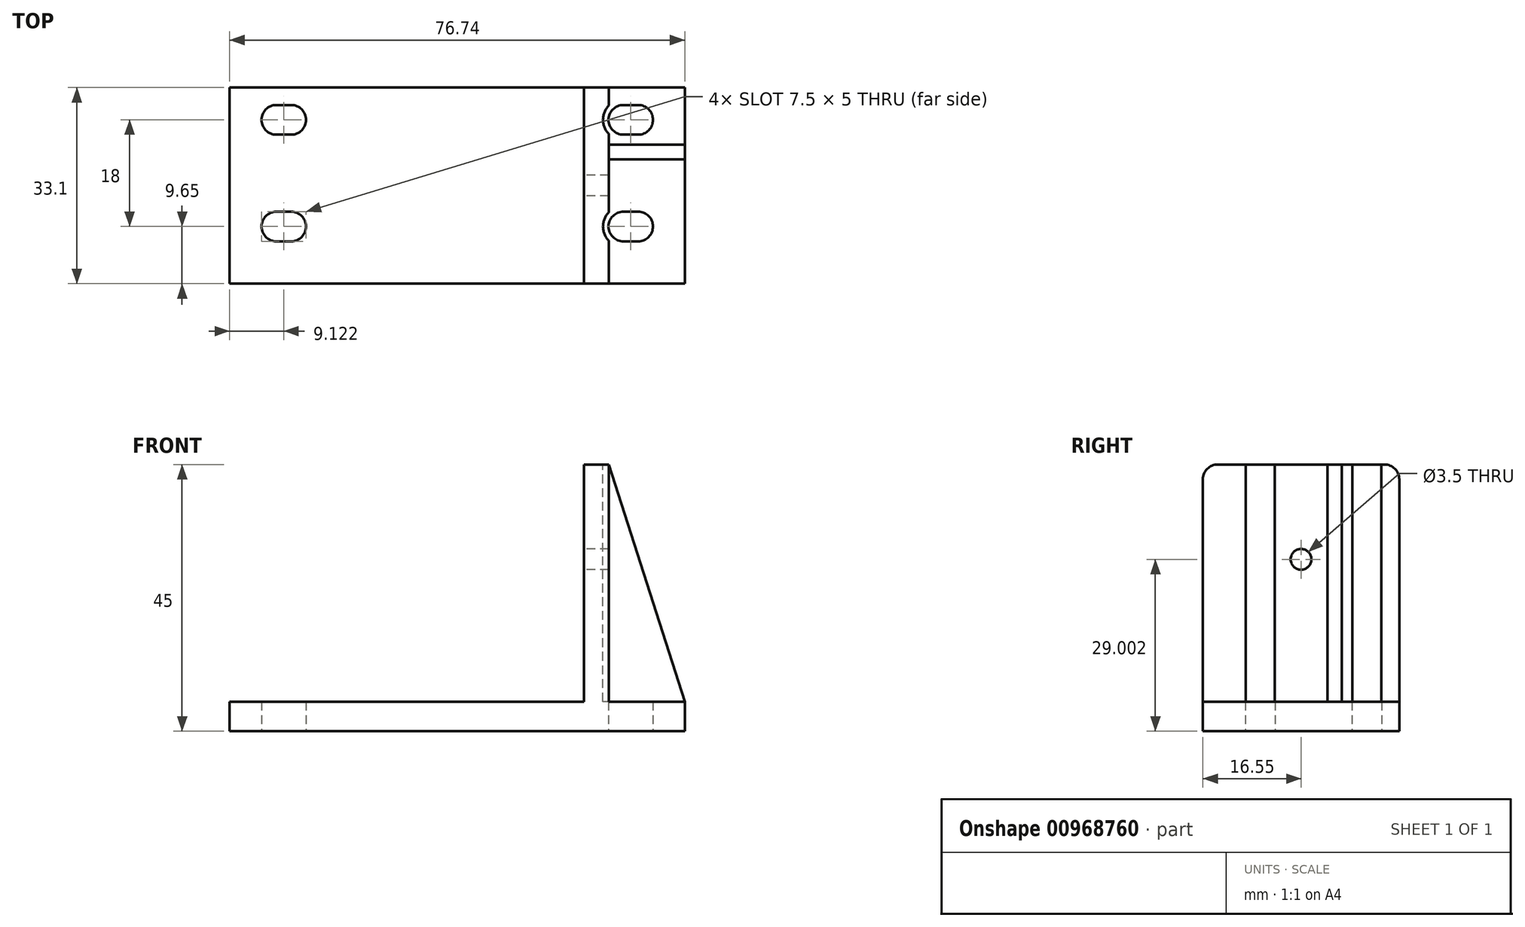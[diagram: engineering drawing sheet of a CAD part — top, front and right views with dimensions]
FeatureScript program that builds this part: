
annotation { "Feature Type Name" : "Feature", "Feature Type Description" : "" }
export const myFeature = defineFeature(function(context is Context, id is Id, definition is map)
    precondition{}
    {
        {
            var Q0;
            Q0=qCreatedBy(makeId("Front.planeOp"),FACE);
            var sketch = newSketch(context, id + "F0", { "sketchPlane" : qUnion([Q0])});
            skCircle(sketch, "E0", {"center": v(17.73, -4.86) * mm, "radius": 4 * mm});
            skLineSegment(sketch, "E1.bottom", {"start": v(0.73, 6.14) * mm, "end": v(34.73, 6.14) * mm});
            skLineSegment(sketch, "E1.top", {"start": v(0.73, -15.86) * mm, "end": v(34.73, -15.86) * mm});
            skLineSegment(sketch, "E1.left", {"start": v(0.73, 6.14) * mm, "end": v(0.73, -15.86) * mm});
            skLineSegment(sketch, "E1.right", {"start": v(34.73, 6.14) * mm, "end": v(34.73, -15.86) * mm});
            skPoint(sketch, "E2.MirrorP", {"position": v(-19.07, -4.86) * mm});
            skLineSegment(sketch, "E3.MirrorCS", {"start": v(-2.07, 6.14) * mm, "end": v(-2.07, -15.86) * mm});
            skLineSegment(sketch, "E4.MirrorCS", {"start": v(-2.07, 6.14) * mm, "end": v(-36.07, 6.14) * mm});
            skLineSegment(sketch, "E5.MirrorCS", {"start": v(-2.07, -15.86) * mm, "end": v(-36.07, -15.86) * mm});
            skLineSegment(sketch, "E6.MirrorCS", {"start": v(-36.07, 6.14) * mm, "end": v(-36.07, -15.86) * mm});
            skCircle(sketch, "E7.MirrorC", {"center": v(-19.07, -4.86) * mm, "radius": 4 * mm});
            skPoint(sketch, "E8.MirrorCS.start.orphan", {"position": v(-19.07, 25.28) * mm});
            skPoint(sketch, "E9.orphan", {"position": v(-23.47, 25.28) * mm});
            skPoint(sketch, "E10.MirrorCS.end.orphan", {"position": v(-23.47, -17.2) * mm});
            skPoint(sketch, "E11.orphan", {"position": v(-19.07, -16.86) * mm});
            skPoint(sketch, "E12.orphan", {"position": v(17.73, -16.86) * mm});
            skPoint(sketch, "E13.orphan", {"position": v(22.13, -17.2) * mm});
            skPoint(sketch, "E14.start.orphan", {"position": v(17.73, 25.28) * mm});
            skPoint(sketch, "E15.orphan", {"position": v(13.33, 25.28) * mm});
            skPoint(sketch, "E16.end.orphan", {"position": v(22.13, 25.28) * mm});
            skSolve(sketch);
        }
        {
            var Q0;
            Q0=makeQuery(id+"F0.imprint","IMPRINT",FACE,{"disambiguationData":[TD([[makeQuery(id+"F0.imprint","IMPRINT",EDGE,{"derivedFrom":sQuery(id+"F0.wireOp",EDGE,"E3.MirrorCS")}),-1.0]])]});
            var Q1;
            Q1=makeQuery(id+"F0.imprint","IMPRINT",FACE,{"disambiguationData":[TD([[makeQuery(id+"F0.imprint","IMPRINT",EDGE,{"derivedFrom":sQuery(id+"F0.wireOp",EDGE,"E0")}),-1.0]])]});
            extrude(context, id + "F1", {"entities" : qUnion([Q0, Q1]), "depth" : 30.2 * mm, "offsetDistance" : 25 * mm});
        }
        {
            var Q0;
            Q0=makeQuery(id+"F1.opExtrude","SWEPT_FACE",FACE,{"disambiguationData":[OSD([sQuery(id+"F0.wireOp",EDGE,"E1.bottom")])]});
            var sketch = newSketch(context, id + "F2", { "sketchPlane" : qUnion([Q0])});
            skArc(sketch, "E17", {"start": v(27.95, -24.5) * mm, "mid": v(30.45, -22) * mm, "end": v(27.95, -19.5) * mm});
            skArc(sketch, "E18.MirrorC", {"start": v(-33.05, -6.5) * mm, "mid": v(-35.55, -4) * mm, "end": v(-33.05, -1.5) * mm});
            skArc(sketch, "E19.MirrorC", {"start": v(-33.05, -24.5) * mm, "mid": v(-35.55, -22) * mm, "end": v(-33.05, -19.5) * mm});
            skLineSegment(sketch, "E20.bottom", {"start": v(-40.92, 1.45) * mm, "end": v(35.82, 1.45) * mm});
            skLineSegment(sketch, "E20.top", {"start": v(-40.92, -31.65) * mm, "end": v(35.82, -31.65) * mm});
            skLineSegment(sketch, "E20.left", {"start": v(-40.92, 1.45) * mm, "end": v(-40.92, -31.65) * mm});
            skLineSegment(sketch, "E20.right", {"start": v(35.82, 1.45) * mm, "end": v(35.82, -31.65) * mm});
            skLineSegment(sketch, "E21", {"start": v(-2.55, 1.45) * mm, "end": v(-2.55, 6.82) * mm});
            skArc(sketch, "E22", {"start": v(-30.55, -6.5) * mm, "mid": v(-28.05, -4) * mm, "end": v(-30.55, -1.5) * mm});
            skArc(sketch, "E23", {"start": v(-30.55, -24.5) * mm, "mid": v(-28.05, -22) * mm, "end": v(-30.55, -19.5) * mm});
            skArc(sketch, "E24.MirrorC", {"start": v(25.45, -24.5) * mm, "mid": v(22.95, -22) * mm, "end": v(25.45, -19.5) * mm});
            skLineSegment(sketch, "E25", {"start": v(-33.05, -1.5) * mm, "end": v(-30.55, -1.5) * mm});
            skLineSegment(sketch, "E26.MirrorCS", {"start": v(-33.05, -6.5) * mm, "end": v(-30.55, -6.5) * mm});
            skLineSegment(sketch, "E27", {"start": v(-33.05, -19.5) * mm, "end": v(-30.55, -19.5) * mm});
            skLineSegment(sketch, "E28.MirrorCS", {"start": v(-33.05, -24.5) * mm, "end": v(-30.55, -24.5) * mm});
            skLineSegment(sketch, "E29.MirrorCS", {"start": v(27.95, -1.5) * mm, "end": v(25.45, -1.5) * mm});
            skLineSegment(sketch, "E30.MirrorCS", {"start": v(27.95, -6.5) * mm, "end": v(25.45, -6.5) * mm});
            skLineSegment(sketch, "E31.MirrorCS", {"start": v(27.95, -19.5) * mm, "end": v(25.45, -19.5) * mm});
            skLineSegment(sketch, "E32.MirrorCS", {"start": v(27.95, -24.5) * mm, "end": v(25.45, -24.5) * mm});
            skArc(sketch, "E33.trimOffspring", {"start": v(25.45, -6.5) * mm, "mid": v(22.95, -4) * mm, "end": v(25.45, -1.5) * mm});
            skArc(sketch, "E34.trimOffspring", {"start": v(27.95, -6.5) * mm, "mid": v(30.45, -4) * mm, "end": v(27.95, -1.5) * mm});
            skSolve(sketch);
        }
        {
            var Q0;
            Q0 = qSketchRegion(id + "F2", true);
            extrude(context, id + "F3", {"entities" : qUnion([Q0]), "depth" : 5 * mm, "offsetDistance" : 25 * mm});
        }
        {
            var Q0;
            Q0=makeQuery(id+"F3.opExtrude","CAP_FACE",FACE,{"disambiguationData":[OSD([sQuery(id+"F2.wireOp",EDGE,"Vzwq34H6-myRi-gqAu-aAAv-NHu5hSRbaYRA"),sQuery(id+"F2.wireOp",EDGE,"E17"),sQuery(id+"F2.wireOp",EDGE,"E18.MirrorC"),sQuery(id+"F2.wireOp",EDGE,"E19.MirrorC"),sQuery(id+"F2.wireOp",EDGE,"E20.bottom"),sQuery(id+"F2.wireOp",EDGE,"E20.top"),sQuery(id+"F2.wireOp",EDGE,"E20.left"),sQuery(id+"F2.wireOp",EDGE,"E20.right")])],"isStart":false});
            var sketch = newSketch(context, id + "F4", { "sketchPlane" : qUnion([Q0])});
            skLineSegment(sketch, "E35", {"start": v(35.82, -15.1) * mm, "end": v(15.82, -15.1) * mm, "construction": true});
            skLineSegment(sketch, "E36.bottom", {"start": v(15.82, -31.65) * mm, "end": v(23.04, -31.65) * mm});
            skLineSegment(sketch, "E36.top", {"start": v(15.82, 1.45) * mm, "end": v(23.04, 1.45) * mm});
            skLineSegment(sketch, "E36.left", {"start": v(15.82, -31.65) * mm, "end": v(15.82, 1.45) * mm});
            skLineSegment(sketch, "E36.right", {"start": v(23.04, -31.65) * mm, "end": v(23.04, 1.45) * mm});
            skSolve(sketch);
        }
        {
            var Q0;
            Q0 = qSketchRegion(id + "F4", true);
            extrude(context, id + "F5", {"entities" : qUnion([Q0]), "operationType" : NewBodyOperationType.ADD, "depth" : 40 * mm, "offsetDistance" : 25 * mm});
        }
        {
            var Q0;
            Q0=makeQuery(id+"F5.opExtrude","SWEPT_FACE",FACE,{"disambiguationData":[OSD([sQuery(id+"F4.wireOp",EDGE,"E36.left")])]});
            var sketch = newSketch(context, id + "F6", { "sketchPlane" : qUnion([Q0])});
            skLineSegment(sketch, "E37", {"start": v(15.1, 11.14) * mm, "end": v(15.1, 35.14) * mm});
            skCircle(sketch, "E38", {"center": v(15.1, 35.14) * mm, "radius": 1.75 * mm});
            skSolve(sketch);
        }
        {
            var Q0;
            Q0 = qSketchRegion(id + "F6", true);
            extrude(context, id + "F7", {"entities" : qUnion([Q0]), "operationType" : NewBodyOperationType.REMOVE, "oppositeDirection" : true, "depth" : 25 * mm, "offsetDistance" : 25 * mm});
        }
        {
            var Q0;
            Q0=makeQuery(id+"F5.opExtrude","CAP_EDGE",EDGE,{"disambiguationData":[OSD([sQuery(id+"F4.wireOp",EDGE,"E36.top")])],"isStart":false});
            var Q1;
            Q1=makeQuery(id+"F5.opExtrude","CAP_EDGE",EDGE,{"disambiguationData":[OSD([sQuery(id+"F4.wireOp",EDGE,"E36.bottom")])],"isStart":false});
            fillet(context, id + "F8", {"entities" : qUnion([Q0, Q1]), "radius" : 2.5 * mm, "tangentPropagation" : true, "allowEdgeOverflow" : false});
        }
        {
            var Q0;
            Q0=makeQuery(id+"F5.opExtrude","CAP_FACE",FACE,{"disambiguationData":[OSD([sQuery(id+"F4.wireOp",EDGE,"E36.bottom"),sQuery(id+"F4.wireOp",EDGE,"E36.top"),sQuery(id+"F4.wireOp",EDGE,"E36.left"),sQuery(id+"F4.wireOp",EDGE,"E36.right")])],"isStart":false});
            var sketch = newSketch(context, id + "F9", { "sketchPlane" : qUnion([Q0])});
            skCircle(sketch, "E39", {"center": v(25.45, -4) * mm, "radius": 3.43 * mm});
            skPoint(sketch, "E40.start.orphan", {"position": v(23.04, -15.1) * mm});
            skCircle(sketch, "E41", {"center": v(25.45, -22) * mm, "radius": 3.43 * mm});
            skSolve(sketch);
        }
        {
            var Q0;
            Q0 = qSketchRegion(id + "F9", true);
            var Q1;
            {var subQ0=sQuery(id+"F2.wireOp",EDGE,"E33.trimOffspring");var subQ1=sQuery(id+"F2.wireOp",EDGE,"E31.MirrorCS");var subQ2=sQuery(id+"F2.wireOp",EDGE,"E24.MirrorC");var subQ3=sQuery(id+"F2.wireOp",EDGE,"E17");var subQ4=sQuery(id+"F2.wireOp",EDGE,"E29.MirrorCS");var subQ5=sQuery(id+"F2.wireOp",EDGE,"E20.bottom");var subQ9=sQuery(id+"F2.wireOp",EDGE,"E30.MirrorCS");var subQ10=sQuery(id+"F2.wireOp",EDGE,"E20.top");var subQ11=sQuery(id+"F2.wireOp",EDGE,"E32.MirrorCS");var subQ12=sQuery(id+"F2.wireOp",EDGE,"E20.right");var subQ13=sQuery(id+"F2.wireOp",EDGE,"E34.trimOffspring");Q1=makeQuery(id+"F5.boolean.opBoolean","SPLIT",FACE,{"disambiguationData":[TD([makeQuery(id+"F3.opExtrude","SWEPT_FACE",FACE,{"disambiguationData":[OSD([subQ3])]})])],"derivedFrom":makeQuery(id+"F3.opExtrude","CAP_FACE",FACE,{"disambiguationData":[OSD([subQ3,sQuery(id+"F2.wireOp",EDGE,"E18.MirrorC"),sQuery(id+"F2.wireOp",EDGE,"E19.MirrorC"),subQ5,subQ10,sQuery(id+"F2.wireOp",EDGE,"E20.left"),subQ12,sQuery(id+"F2.wireOp",EDGE,"E22"),sQuery(id+"F2.wireOp",EDGE,"E23"),subQ2,sQuery(id+"F2.wireOp",EDGE,"E25"),sQuery(id+"F2.wireOp",EDGE,"E26.MirrorCS"),sQuery(id+"F2.wireOp",EDGE,"E27"),sQuery(id+"F2.wireOp",EDGE,"E28.MirrorCS"),subQ4,subQ9,subQ1,subQ11,subQ0,subQ13])],"isStart":false})});}
            extrude(context, id + "F10", {"entities" : qUnion([Q0]), "operationType" : NewBodyOperationType.REMOVE, "endBound" : BoundingType.UP_TO_SURFACE, "oppositeDirection" : true, "depth" : 25 * mm, "endBoundEntityFace" : qUnion([Q1]), "offsetDistance" : 25 * mm});
        }
        {
            var Q0;
            Q0=makeQuery(id+"F3.opExtrude","SWEPT_BODY",BODY,{"disambiguationData":[OSD([sQuery(id+"F2.wireOp",EDGE,"E17"),sQuery(id+"F2.wireOp",EDGE,"E18.MirrorC"),sQuery(id+"F2.wireOp",EDGE,"E19.MirrorC"),sQuery(id+"F2.wireOp",EDGE,"E20.bottom"),sQuery(id+"F2.wireOp",EDGE,"E20.top"),sQuery(id+"F2.wireOp",EDGE,"E20.left"),sQuery(id+"F2.wireOp",EDGE,"E20.right"),sQuery(id+"F2.wireOp",EDGE,"E22"),sQuery(id+"F2.wireOp",EDGE,"E23"),sQuery(id+"F2.wireOp",EDGE,"E24.MirrorC"),sQuery(id+"F2.wireOp",EDGE,"E25"),sQuery(id+"F2.wireOp",EDGE,"E26.MirrorCS"),sQuery(id+"F2.wireOp",EDGE,"E27"),sQuery(id+"F2.wireOp",EDGE,"E28.MirrorCS"),sQuery(id+"F2.wireOp",EDGE,"E29.MirrorCS"),sQuery(id+"F2.wireOp",EDGE,"E30.MirrorCS"),sQuery(id+"F2.wireOp",EDGE,"E31.MirrorCS"),sQuery(id+"F2.wireOp",EDGE,"E32.MirrorCS"),sQuery(id+"F2.wireOp",EDGE,"E33.trimOffspring"),sQuery(id+"F2.wireOp",EDGE,"E34.trimOffspring")])]});
            transform(context, id + "F11", {"entities" : qUnion([Q0]), "transformType" : TransformType.TRANSLATION_3D, "dx" : 0 * mm, "dy" : 0 * mm, "dz" : 0 * mm, "makeCopy" : true});
        }
        {
            var Q0;
            Q0=makeQuery(id+"F11.opPattern","COPY",BODY,{"derivedFrom":makeQuery(id+"F3.opExtrude","SWEPT_BODY",BODY,{"disambiguationData":[OSD([sQuery(id+"F2.wireOp",EDGE,"E17"),sQuery(id+"F2.wireOp",EDGE,"E18.MirrorC"),sQuery(id+"F2.wireOp",EDGE,"E19.MirrorC"),sQuery(id+"F2.wireOp",EDGE,"E20.bottom"),sQuery(id+"F2.wireOp",EDGE,"E20.top"),sQuery(id+"F2.wireOp",EDGE,"E20.left"),sQuery(id+"F2.wireOp",EDGE,"E20.right"),sQuery(id+"F2.wireOp",EDGE,"E22"),sQuery(id+"F2.wireOp",EDGE,"E23"),sQuery(id+"F2.wireOp",EDGE,"E24.MirrorC"),sQuery(id+"F2.wireOp",EDGE,"E25"),sQuery(id+"F2.wireOp",EDGE,"E26.MirrorCS"),sQuery(id+"F2.wireOp",EDGE,"E27"),sQuery(id+"F2.wireOp",EDGE,"E28.MirrorCS"),sQuery(id+"F2.wireOp",EDGE,"E29.MirrorCS"),sQuery(id+"F2.wireOp",EDGE,"E30.MirrorCS"),sQuery(id+"F2.wireOp",EDGE,"E31.MirrorCS"),sQuery(id+"F2.wireOp",EDGE,"E32.MirrorCS"),sQuery(id+"F2.wireOp",EDGE,"E33.trimOffspring"),sQuery(id+"F2.wireOp",EDGE,"E34.trimOffspring")])]}),"instanceName":"1"});
            deleteBodies(context, id + "F12", {"entities" : qUnion([Q0])});
        }
        {
            var Q0;
            Q0=makeQuery(id+"F1.opExtrude","SWEPT_BODY",BODY,{"disambiguationData":[OSD([sQuery(id+"F0.wireOp",EDGE,"E0"),sQuery(id+"F0.wireOp",EDGE,"E1.bottom"),sQuery(id+"F0.wireOp",EDGE,"E1.top"),sQuery(id+"F0.wireOp",EDGE,"E1.left"),sQuery(id+"F0.wireOp",EDGE,"E1.right")])]});
            var Q1;
            Q1=makeQuery(id+"F1.opExtrude","SWEPT_BODY",BODY,{"disambiguationData":[OSD([sQuery(id+"F0.wireOp",EDGE,"E3.MirrorCS"),sQuery(id+"F0.wireOp",EDGE,"E4.MirrorCS"),sQuery(id+"F0.wireOp",EDGE,"E5.MirrorCS"),sQuery(id+"F0.wireOp",EDGE,"E6.MirrorCS"),sQuery(id+"F0.wireOp",EDGE,"E7.MirrorC")])]});
            deleteBodies(context, id + "F13", {"entities" : qUnion([Q0, Q1])});
        }
        {
            var Q0;
            Q0=makeQuery(id+"F5.opExtrude","CAP_FACE",FACE,{"disambiguationData":[OSD([sQuery(id+"F4.wireOp",EDGE,"E36.bottom"),sQuery(id+"F4.wireOp",EDGE,"E36.top"),sQuery(id+"F4.wireOp",EDGE,"E36.left"),sQuery(id+"F4.wireOp",EDGE,"E36.right")])],"isStart":false});
            var sketch = newSketch(context, id + "F14", { "sketchPlane" : qUnion([Q0])});
            skPoint(sketch, "E42.oppositeSnap0", {"position": v(18.82, -29.15) * mm});
            skLineSegment(sketch, "E42.bottom", {"start": v(15.82, 1.45) * mm, "end": v(18.82, 1.45) * mm});
            skLineSegment(sketch, "E42.top", {"start": v(15.82, -31.65) * mm, "end": v(18.82, -31.65) * mm});
            skLineSegment(sketch, "E42.left", {"start": v(15.82, 1.45) * mm, "end": v(15.82, -31.65) * mm});
            skLineSegment(sketch, "E42.right", {"start": v(18.82, 1.45) * mm, "end": v(18.82, -31.65) * mm});
            skSolve(sketch);
        }
        {
            var Q0;
            Q0 = qSketchRegion(id + "F14", true);
            var Q1;
            {var subQ0=sQuery(id+"F2.wireOp",EDGE,"E26.MirrorCS");var subQ1=sQuery(id+"F2.wireOp",EDGE,"E25");var subQ2=sQuery(id+"F2.wireOp",EDGE,"E23");var subQ3=sQuery(id+"F2.wireOp",EDGE,"E22");var subQ4=sQuery(id+"F2.wireOp",EDGE,"E20.left");var subQ5=sQuery(id+"F2.wireOp",EDGE,"E27");var subQ6=sQuery(id+"F2.wireOp",EDGE,"E18.MirrorC");var subQ7=sQuery(id+"F2.wireOp",EDGE,"E19.MirrorC");var subQ8=sQuery(id+"F2.wireOp",EDGE,"E20.bottom");var subQ9=sQuery(id+"F2.wireOp",EDGE,"E20.top");var subQ10=sQuery(id+"F2.wireOp",EDGE,"E28.MirrorCS");Q1=makeQuery(id+"F5.boolean.opBoolean","SPLIT",FACE,{"disambiguationData":[TD([makeQuery(id+"F3.opExtrude","SWEPT_FACE",FACE,{"disambiguationData":[OSD([subQ6])]})])],"derivedFrom":makeQuery(id+"F3.opExtrude","CAP_FACE",FACE,{"disambiguationData":[OSD([sQuery(id+"F2.wireOp",EDGE,"E17"),subQ6,subQ7,subQ8,subQ9,subQ4,sQuery(id+"F2.wireOp",EDGE,"E20.right"),subQ3,subQ2,sQuery(id+"F2.wireOp",EDGE,"E24.MirrorC"),subQ1,subQ0,subQ5,subQ10,sQuery(id+"F2.wireOp",EDGE,"E29.MirrorCS"),sQuery(id+"F2.wireOp",EDGE,"E30.MirrorCS"),sQuery(id+"F2.wireOp",EDGE,"E31.MirrorCS"),sQuery(id+"F2.wireOp",EDGE,"E32.MirrorCS"),sQuery(id+"F2.wireOp",EDGE,"E33.trimOffspring"),sQuery(id+"F2.wireOp",EDGE,"E34.trimOffspring")])],"isStart":false})});}
            extrude(context, id + "F15", {"entities" : qUnion([Q0]), "operationType" : NewBodyOperationType.REMOVE, "endBound" : BoundingType.UP_TO_SURFACE, "oppositeDirection" : true, "depth" : 25 * mm, "endBoundEntityFace" : qUnion([Q1]), "offsetDistance" : 25 * mm});
        }
        {
            var Q0;
            {var subQ0=sQuery(id+"F2.wireOp",EDGE,"E33.trimOffspring");var subQ1=sQuery(id+"F2.wireOp",EDGE,"E31.MirrorCS");var subQ2=sQuery(id+"F2.wireOp",EDGE,"E24.MirrorC");var subQ3=sQuery(id+"F2.wireOp",EDGE,"E17");var subQ4=sQuery(id+"F2.wireOp",EDGE,"E29.MirrorCS");var subQ5=sQuery(id+"F2.wireOp",EDGE,"E20.bottom");var subQ9=sQuery(id+"F2.wireOp",EDGE,"E30.MirrorCS");var subQ10=sQuery(id+"F2.wireOp",EDGE,"E20.top");var subQ11=sQuery(id+"F2.wireOp",EDGE,"E32.MirrorCS");var subQ12=sQuery(id+"F2.wireOp",EDGE,"E20.right");var subQ13=sQuery(id+"F2.wireOp",EDGE,"E34.trimOffspring");Q0=makeQuery(id+"F10.boolean.opBoolean","MERGE",FACE,{"derivedFrom":[makeQuery(id+"F5.boolean.opBoolean","SPLIT",FACE,{"disambiguationData":[TD([makeQuery(id+"F3.opExtrude","SWEPT_FACE",FACE,{"disambiguationData":[OSD([subQ3])]})])],"derivedFrom":makeQuery(id+"F3.opExtrude","CAP_FACE",FACE,{"disambiguationData":[OSD([subQ3,sQuery(id+"F2.wireOp",EDGE,"E18.MirrorC"),sQuery(id+"F2.wireOp",EDGE,"E19.MirrorC"),subQ5,subQ10,sQuery(id+"F2.wireOp",EDGE,"E20.left"),subQ12,sQuery(id+"F2.wireOp",EDGE,"E22"),sQuery(id+"F2.wireOp",EDGE,"E23"),subQ2,sQuery(id+"F2.wireOp",EDGE,"E25"),sQuery(id+"F2.wireOp",EDGE,"E26.MirrorCS"),sQuery(id+"F2.wireOp",EDGE,"E27"),sQuery(id+"F2.wireOp",EDGE,"E28.MirrorCS"),subQ4,subQ9,subQ1,subQ11,subQ0,subQ13])],"isStart":false})})],"fromTools":[makeQuery(id+"F10.opExtrude","CAP_FACE",FACE,{"disambiguationData":[OSD([sQuery(id+"F9.wireOp",EDGE,"E39")])],"isStart":false}),makeQuery(id+"F10.opExtrude","CAP_FACE",FACE,{"disambiguationData":[OSD([sQuery(id+"F9.wireOp",EDGE,"E41")])],"isStart":false})]});}
            var sketch = newSketch(context, id + "F16", { "sketchPlane" : qUnion([Q0])});
            skLineSegment(sketch, "E43.bottom", {"start": v(23.04, -8.22) * mm, "end": v(35.82, -8.22) * mm});
            skLineSegment(sketch, "E43.top", {"start": v(23.04, -10.68) * mm, "end": v(35.82, -10.68) * mm});
            skLineSegment(sketch, "E43.left", {"start": v(23.04, -8.22) * mm, "end": v(23.04, -10.68) * mm});
            skLineSegment(sketch, "E43.right", {"start": v(35.82, -8.22) * mm, "end": v(35.82, -10.68) * mm});
            skSolve(sketch);
        }
        {
            var Q0;
            Q0 = qSketchRegion(id + "F16", true);
            var Q1;
            Q1=makeQuery(id+"F5.opExtrude","CAP_FACE",FACE,{"disambiguationData":[OSD([sQuery(id+"F4.wireOp",EDGE,"E36.bottom"),sQuery(id+"F4.wireOp",EDGE,"E36.top"),sQuery(id+"F4.wireOp",EDGE,"E36.left"),sQuery(id+"F4.wireOp",EDGE,"E36.right")])],"isStart":false});
            extrude(context, id + "F17", {"entities" : qUnion([Q0]), "operationType" : NewBodyOperationType.ADD, "endBound" : BoundingType.UP_TO_SURFACE, "depth" : 25 * mm, "endBoundEntityFace" : qUnion([Q1]), "offsetDistance" : 25 * mm});
        }
        {
            var Q0;
            Q0=makeQuery(id+"F17.opExtrude","SWEPT_FACE",FACE,{"disambiguationData":[OSD([sQuery(id+"F16.wireOp",EDGE,"E43.top")])]});
            var sketch = newSketch(context, id + "F18", { "sketchPlane" : qUnion([Q0])});
            skLineSegment(sketch, "E44", {"start": v(23.04, 51.14) * mm, "end": v(35.82, 11.14) * mm});
            skLineSegment(sketch, "E45", {"start": v(35.82, 11.14) * mm, "end": v(35.82, 51.14) * mm});
            skLineSegment(sketch, "E46", {"start": v(35.82, 51.14) * mm, "end": v(23.04, 51.14) * mm});
            skSolve(sketch);
        }
        {
            var Q0;
            Q0 = qSketchRegion(id + "F18", true);
            extrude(context, id + "F19", {"entities" : qUnion([Q0]), "operationType" : NewBodyOperationType.REMOVE, "oppositeDirection" : true, "depth" : 25 * mm, "offsetDistance" : 25 * mm});
        }
    });
